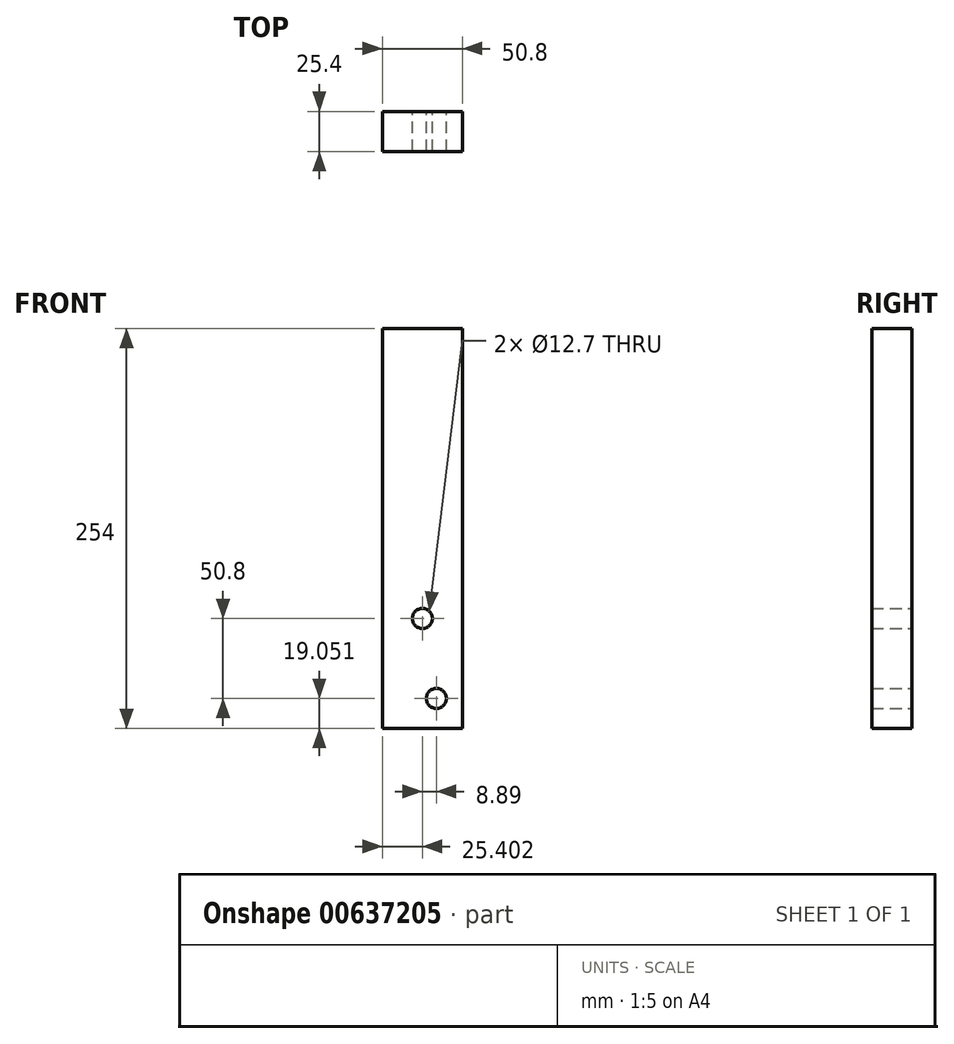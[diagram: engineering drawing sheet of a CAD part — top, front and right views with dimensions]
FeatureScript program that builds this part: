
annotation { "Feature Type Name" : "Feature", "Feature Type Description" : "" }
export const myFeature = defineFeature(function(context is Context, id is Id, definition is map)
    precondition{}
    {
        {
            var Q0;
            Q0=qCreatedBy(makeId("Front.planeOp"),FACE);
            var sketch = newSketch(context, id + "F0", { "sketchPlane" : qUnion([Q0])});
            skLineSegment(sketch, "E0.bottom", {"start": v(-45.35, 185.32) * mm, "end": v(5.45, 185.32) * mm});
            skLineSegment(sketch, "E0.top", {"start": v(-45.35, -68.68) * mm, "end": v(5.45, -68.68) * mm});
            skLineSegment(sketch, "E0.left", {"start": v(-45.35, 185.32) * mm, "end": v(-45.35, -68.68) * mm});
            skLineSegment(sketch, "E0.right", {"start": v(5.45, 185.32) * mm, "end": v(5.45, -68.68) * mm});
            skCircle(sketch, "E1", {"center": v(-11.06, -49.63) * mm, "radius": 6.35 * mm});
            skCircle(sketch, "E2", {"center": v(-19.95, 1.17) * mm, "radius": 6.35 * mm});
            skSolve(sketch);
        }
        {
            var Q0;
            Q0=makeQuery(id+"F0.imprint","IMPRINT",FACE,{"disambiguationData":[TD([[makeQuery(id+"F0.imprint","IMPRINT",EDGE,{"derivedFrom":sQuery(id+"F0.wireOp",EDGE,"E0.bottom")}),-1.0]])]});
            extrude(context, id + "F1", {"entities" : qUnion([Q0]), "depth" : 25.4 * mm, "offsetDistance" : 25.4 * mm});
        }
    });
